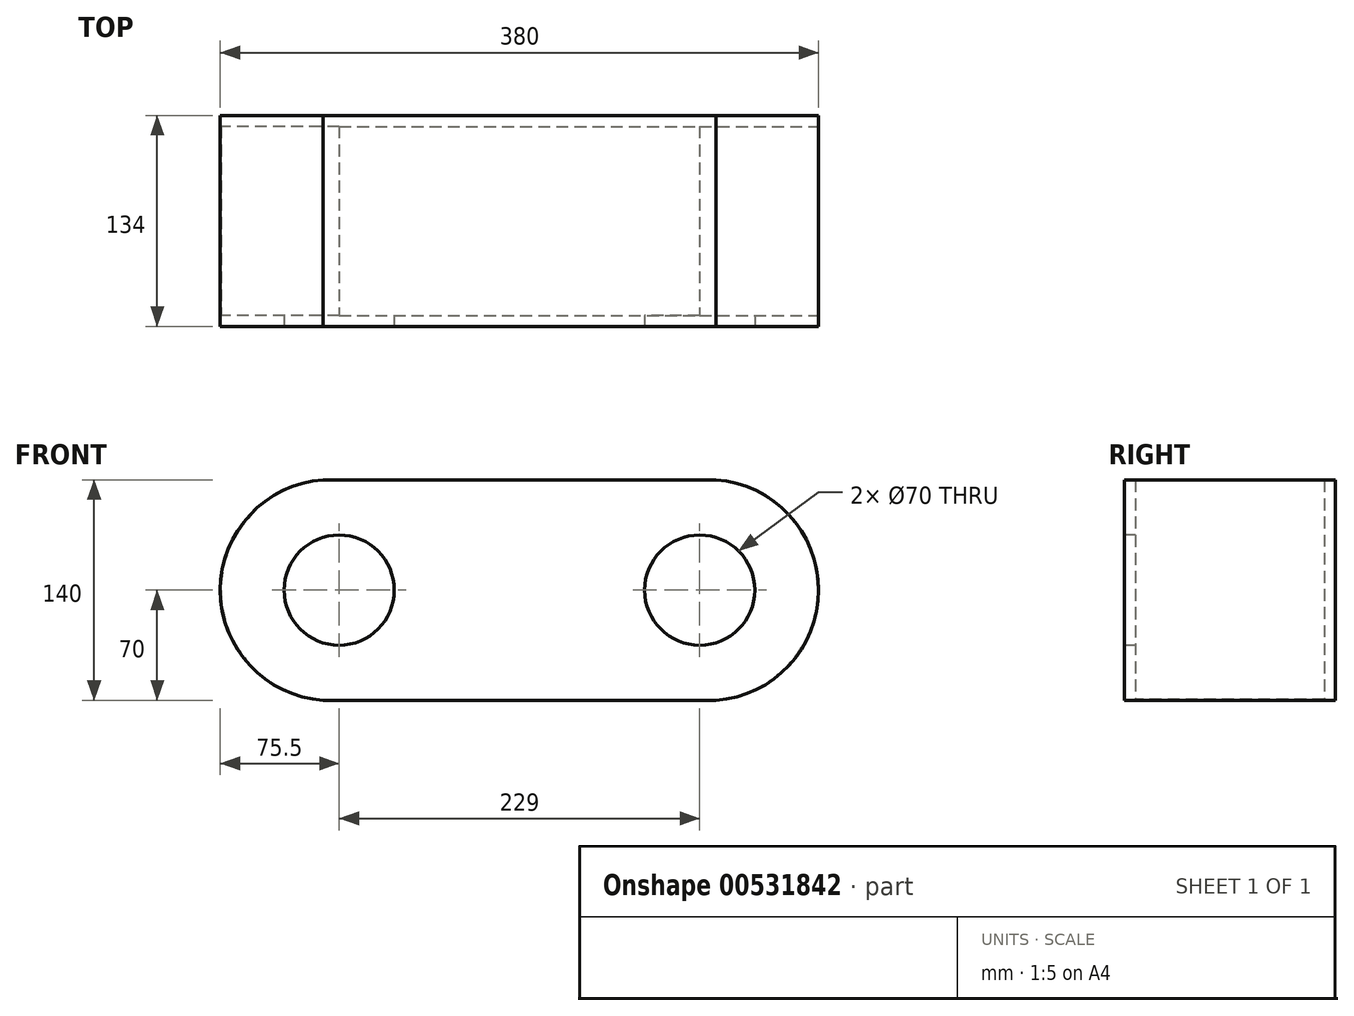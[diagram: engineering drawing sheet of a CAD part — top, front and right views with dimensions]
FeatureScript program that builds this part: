
annotation { "Feature Type Name" : "Feature", "Feature Type Description" : "" }
export const myFeature = defineFeature(function(context is Context, id is Id, definition is map)
    precondition{}
    {
        {
            var Q0;
            Q0=qCreatedBy(makeId("Front.planeOp"),FACE);
            var sketch = newSketch(context, id + "F0", { "sketchPlane" : qUnion([Q0])});
            skLineSegment(sketch, "E0.bottom", {"start": v(-124.67, 70) * mm, "end": v(124.67, 70) * mm});
            skLineSegment(sketch, "E0.top", {"start": v(-124.67, -70) * mm, "end": v(190, -70) * mm});
            skPoint(sketch, "E0.middle", {"position": v(0, 0) * mm});
            skArc(sketch, "E1", {"start": v(-115, 70) * mm, "mid": v(-190, 0) * mm, "end": v(-115, -70) * mm});
            skArc(sketch, "E2", {"start": v(115, -70) * mm, "mid": v(190, 0) * mm, "end": v(115, 70) * mm});
            skPoint(sketch, "E3.orphan", {"position": v(-190, 70) * mm});
            skPoint(sketch, "E4.orphan", {"position": v(-190, -70) * mm});
            skPoint(sketch, "E5.orphan", {"position": v(190, 70) * mm});
            skSolve(sketch);
        }
        {
            var Q0;
            {var subQ0=sQuery(id+"F0.wireOp",EDGE,"E1");var subQ5=sQuery(id+"F0.wireOp",EDGE,"E0.bottom");var subQ9=makeQuery(id+"F0.imprint","INTERSECT",VERTEX,{"disambiguationData":[OD(0.0)],"derivedFrom":[subQ5,subQ0]});Q0=makeQuery(id+"F0.imprint","IMPRINT",FACE,{"disambiguationData":[TD([[makeQuery(id+"F0.imprint","IMPRINT",EDGE,{"disambiguationData":[TD([[subQ9,-1.0]])],"derivedFrom":subQ5}),-1.0]])]});}
            extrude(context, id + "F1", {"entities" : qUnion([Q0]), "oppositeDirection" : true, "depth" : 67 * mm, "offsetDistance" : 25 * mm});
        }
        {
            var Q0;
            Q0=makeQuery(id+"F1.opExtrude","CAP_FACE",FACE,{"disambiguationData":[OSD([sQuery(id+"F0.wireOp",EDGE,"E0.bottom"),sQuery(id+"F0.wireOp",EDGE,"E0.top"),sQuery(id+"F0.wireOp",EDGE,"E1"),sQuery(id+"F0.wireOp",EDGE,"E2")])],"isStart":true});
            var sketch = newSketch(context, id + "F2", { "sketchPlane" : qUnion([Q0])});
            skLineSegment(sketch, "E6.bottom", {"start": v(-125.1, 69.5) * mm, "end": v(125.1, 69.5) * mm});
            skLineSegment(sketch, "E6.top", {"start": v(-125.1, -69.5) * mm, "end": v(125.1, -69.5) * mm});
            skPoint(sketch, "E6.middle", {"position": v(0, 0) * mm});
            skArc(sketch, "E7", {"start": v(-114.5, 69.5) * mm, "mid": v(-189.5, 0) * mm, "end": v(-114.5, -69.5) * mm});
            skArc(sketch, "E8", {"start": v(114.5, -69.5) * mm, "mid": v(189.5, 0) * mm, "end": v(114.5, 69.5) * mm});
            skPoint(sketch, "E9.orphan", {"position": v(-189.5, 69.5) * mm});
            skPoint(sketch, "E10.orphan", {"position": v(-189.5, -69.5) * mm});
            skPoint(sketch, "E11.orphan", {"position": v(189.5, -69.5) * mm});
            skPoint(sketch, "E6.right.start.orphan", {"position": v(189.5, 69.5) * mm});
            skSolve(sketch);
        }
        {
            var Q0;
            Q0 = qSketchRegion(id + "F2", true);
            extrude(context, id + "F3", {"entities" : qUnion([Q0]), "operationType" : NewBodyOperationType.REMOVE, "oppositeDirection" : true, "depth" : 60 * mm, "offsetDistance" : 25 * mm});
        }
        {
            var Q0;
            Q0=makeQuery(id+"F1.opExtrude","SWEPT_BODY",BODY,{"disambiguationData":[OSD([sQuery(id+"F0.wireOp",EDGE,"E0.bottom"),sQuery(id+"F0.wireOp",EDGE,"E0.top"),sQuery(id+"F0.wireOp",EDGE,"E1"),sQuery(id+"F0.wireOp",EDGE,"E2")])]});
            var Q1;
            Q1=makeQuery(id+"F1.opExtrude","CAP_FACE",FACE,{"disambiguationData":[OSD([sQuery(id+"F0.wireOp",EDGE,"E0.bottom"),sQuery(id+"F0.wireOp",EDGE,"E0.top"),sQuery(id+"F0.wireOp",EDGE,"E1"),sQuery(id+"F0.wireOp",EDGE,"E2")])],"isStart":true});
            mirror(context, id + "F4", {"operationType" : NewBodyOperationType.ADD, "entities" : qUnion([Q0]), "mirrorPlane" : qUnion([Q1])});
        }
        {
            var Q0;
            Q0=makeQuery(id+"F4.opPattern","COPY",FACE,{"derivedFrom":makeQuery(id+"F1.opExtrude","CAP_FACE",FACE,{"disambiguationData":[OSD([sQuery(id+"F0.wireOp",EDGE,"E0.bottom"),sQuery(id+"F0.wireOp",EDGE,"E0.top"),sQuery(id+"F0.wireOp",EDGE,"E1"),sQuery(id+"F0.wireOp",EDGE,"E2")])],"isStart":false}),"instanceName":"1"});
            var sketch = newSketch(context, id + "F5", { "sketchPlane" : qUnion([Q0])});
            skCircle(sketch, "E12", {"center": v(-114.5, 0) * mm, "radius": 35 * mm});
            skCircle(sketch, "E13", {"center": v(114.5, 0) * mm, "radius": 35 * mm});
            skSolve(sketch);
        }
        {
            var Q0;
            Q0 = qSketchRegion(id + "F5", true);
            extrude(context, id + "F6", {"entities" : qUnion([Q0]), "operationType" : NewBodyOperationType.REMOVE, "endBound" : BoundingType.UP_TO_NEXT, "oppositeDirection" : true, "depth" : 25 * mm, "offsetDistance" : 25 * mm});
        }
    });
